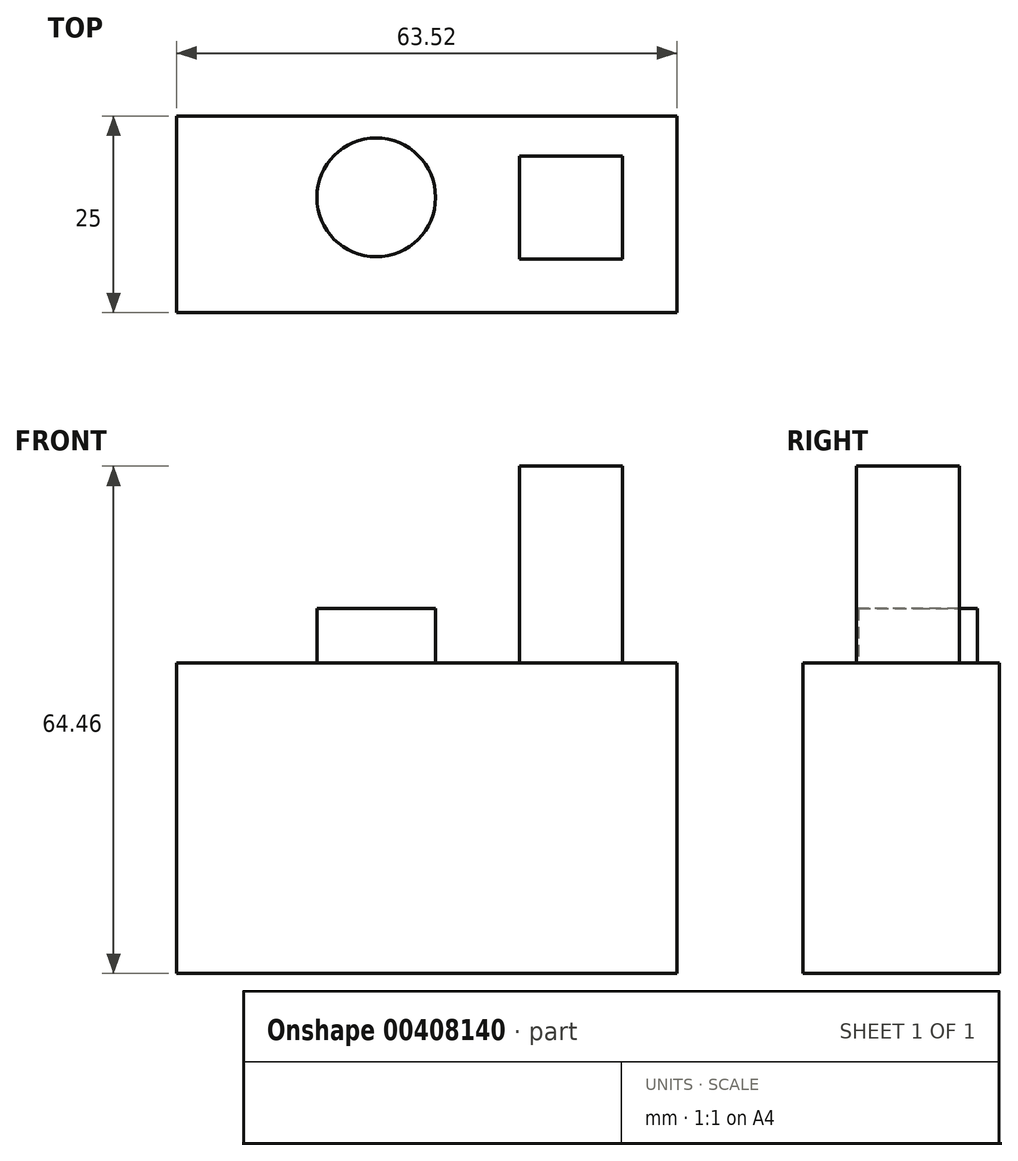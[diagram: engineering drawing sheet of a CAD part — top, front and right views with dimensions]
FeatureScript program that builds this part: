
annotation { "Feature Type Name" : "Feature", "Feature Type Description" : "" }
export const myFeature = defineFeature(function(context is Context, id is Id, definition is map)
    precondition{}
    {
        {
            var Q0;
            Q0=qCreatedBy(makeId("Front.planeOp"),FACE);
            var sketch = newSketch(context, id + "F0", { "sketchPlane" : qUnion([Q0])});
            skLineSegment(sketch, "E0.bottom", {"start": v(0, 0) * mm, "end": v(63.52, 0) * mm});
            skLineSegment(sketch, "E0.top", {"start": v(0, -39.46) * mm, "end": v(63.52, -39.46) * mm});
            skLineSegment(sketch, "E0.left", {"start": v(0, 0) * mm, "end": v(0, -39.46) * mm});
            skLineSegment(sketch, "E0.right", {"start": v(63.52, 0) * mm, "end": v(63.52, -39.46) * mm});
            skSolve(sketch);
        }
        {
            var Q0;
            Q0=makeQuery(id+"F0.imprint","IMPRINT",FACE,{"disambiguationData":[TD([[makeQuery(id+"F0.imprint","IMPRINT",EDGE,{"derivedFrom":sQuery(id+"F0.wireOp",EDGE,"E0.bottom")}),-1.0]])]});
            extrude(context, id + "F1", {"entities" : qUnion([Q0]), "depth" : 25 * mm, "offsetDistance" : 25 * mm});
        }
        {
            var Q0;
            Q0=makeQuery(id+"F1.opExtrude","SWEPT_FACE",FACE,{"disambiguationData":[OSD([sQuery(id+"F0.wireOp",EDGE,"E0.bottom")])]});
            var sketch = newSketch(context, id + "F2", { "sketchPlane" : qUnion([Q0])});
            skCircle(sketch, "E1", {"center": v(25.34, -10.35) * mm, "radius": 7.54 * mm});
            skSolve(sketch);
        }
        {
            var Q0;
            Q0=makeQuery(id+"F2.imprint","IMPRINT",FACE,{"disambiguationData":[TD([[makeQuery(id+"F2.imprint","IMPRINT",EDGE,{"derivedFrom":sQuery(id+"F2.wireOp",EDGE,"E1")}),1.0]])]});
            extrude(context, id + "F3", {"entities" : qUnion([Q0]), "operationType" : NewBodyOperationType.ADD, "depth" : 6.9 * mm, "offsetDistance" : 25 * mm});
        }
        {
            var Q0;
            Q0=makeQuery(id+"F1.opExtrude","SWEPT_FACE",FACE,{"disambiguationData":[OSD([sQuery(id+"F0.wireOp",EDGE,"E0.bottom")])]});
            var sketch = newSketch(context, id + "F4", { "sketchPlane" : qUnion([Q0])});
            skLineSegment(sketch, "E2.bottom", {"start": v(43.55, -5.08) * mm, "end": v(56.65, -5.08) * mm});
            skLineSegment(sketch, "E2.top", {"start": v(43.55, -18.17) * mm, "end": v(56.65, -18.17) * mm});
            skLineSegment(sketch, "E2.left", {"start": v(43.55, -5.08) * mm, "end": v(43.55, -18.17) * mm});
            skLineSegment(sketch, "E2.right", {"start": v(56.65, -5.08) * mm, "end": v(56.65, -18.17) * mm});
            skSolve(sketch);
        }
        {
            var Q0;
            Q0=makeQuery(id+"F4.imprint","IMPRINT",FACE,{"disambiguationData":[TD([[makeQuery(id+"F4.imprint","IMPRINT",EDGE,{"derivedFrom":sQuery(id+"F4.wireOp",EDGE,"E2.bottom")}),-1.0]])]});
            extrude(context, id + "F5", {"entities" : qUnion([Q0]), "operationType" : NewBodyOperationType.ADD, "depth" : 25 * mm, "offsetDistance" : 25 * mm});
        }
    });
